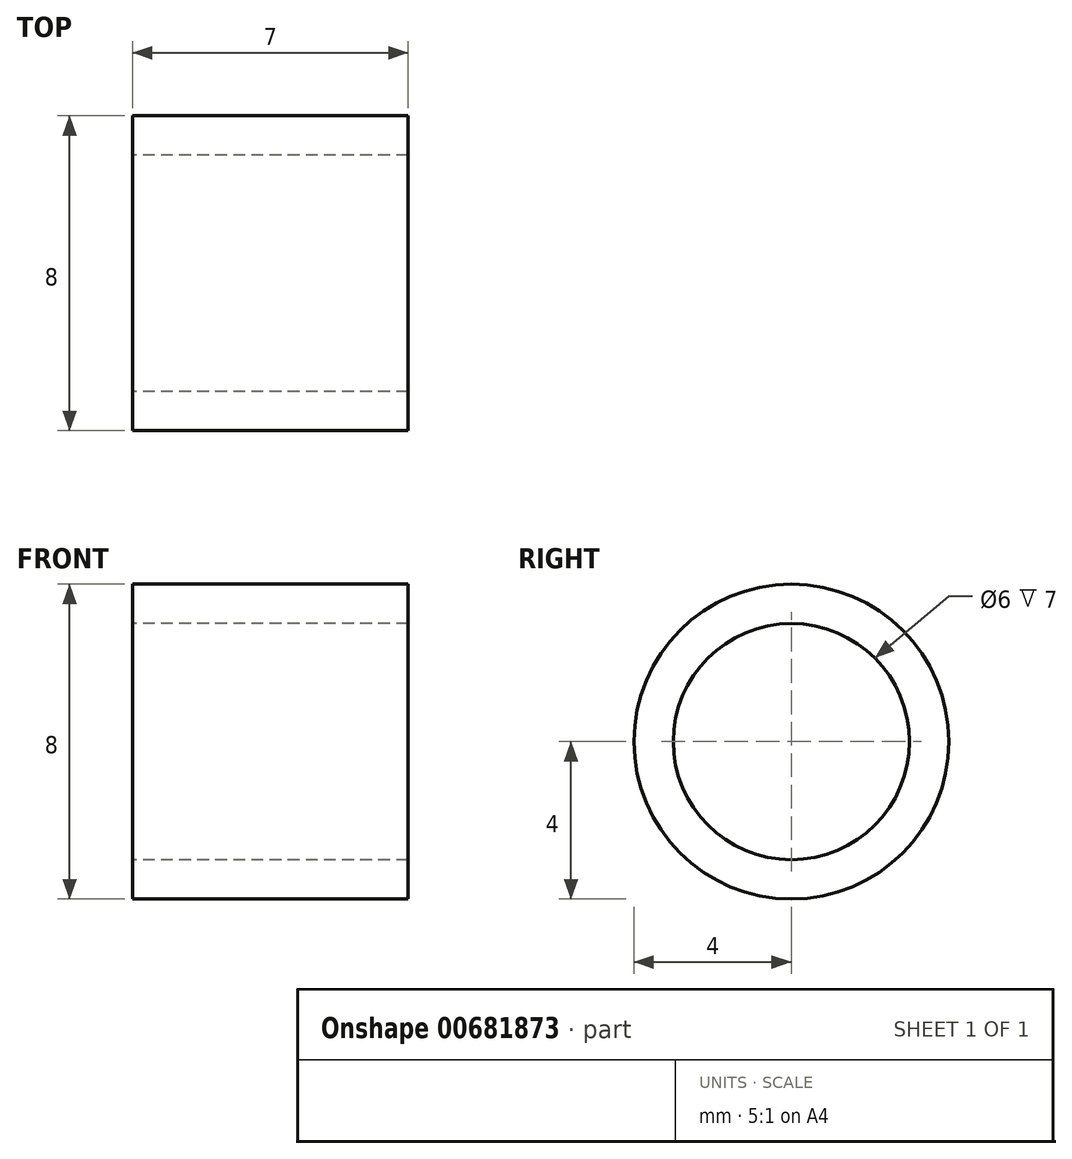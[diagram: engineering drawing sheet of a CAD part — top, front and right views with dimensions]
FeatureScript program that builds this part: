
annotation { "Feature Type Name" : "Feature", "Feature Type Description" : "" }
export const myFeature = defineFeature(function(context is Context, id is Id, definition is map)
    precondition{}
    {
        {
            var Q0;
            Q0=qCreatedBy(makeId("Right.planeOp"),FACE);
            var sketch = newSketch(context, id + "F0", { "sketchPlane" : qUnion([Q0])});
            skCircle(sketch, "E0", {"center": v(0, 0) * mm, "radius": 4 * mm});
            skSolve(sketch);
        }
        {
            var Q0;
            Q0=makeQuery(id+"F0.imprint","IMPRINT",FACE,{"disambiguationData":[TD([[makeQuery(id+"F0.imprint","IMPRINT",EDGE,{"derivedFrom":sQuery(id+"F0.wireOp",EDGE,"E0")}),1.0]])]});
            extrude(context, id + "F1", {"entities" : qUnion([Q0]), "depth" : 7 * mm, "offsetDistance" : 25 * mm});
        }
        {
            var Q0;
            Q0=makeQuery(id+"F1.opExtrude","CAP_FACE",FACE,{"disambiguationData":[OSD([sQuery(id+"F0.wireOp",EDGE,"E0")])],"isStart":false});
            var sketch = newSketch(context, id + "F2", { "sketchPlane" : qUnion([Q0])});
            skPoint(sketch, "E1", {"position": v(0, 0) * mm});
            skSolve(sketch);
        }
        {
            var Q0;
            Q0=sQuery(id+"F2.wireOp",VERTEX,"E1");
            var Q1;
            Q1=makeQuery(id+"F1.opExtrude","SWEPT_BODY",BODY,{"disambiguationData":[OSD([sQuery(id+"F0.wireOp",EDGE,"E0")])]});
            hole(context, id + "F3", {"style" : HoleStyle.SIMPLE, "endStyle" : HoleEndStyle.THROUGH, "holeDiameter" : 6 * mm, "majorDiameter" : 5 * mm, "isTappedThrough" : true, "tappedDepth" : 12 * mm, "tapClearance" : 3, "startFromSketch" : true, "locations" : qUnion([Q0]), "scope" : qUnion([Q1])});
        }
    });
